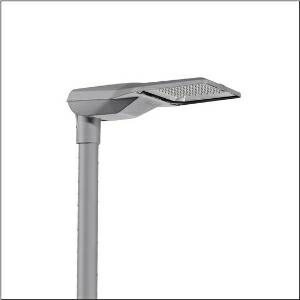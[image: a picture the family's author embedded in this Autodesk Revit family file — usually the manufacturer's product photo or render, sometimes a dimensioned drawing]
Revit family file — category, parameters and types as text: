
# Revit family: streetlight_sl_21_iq_midi___stw1_0a_5xe3e41g08mb_cdbd
name_source: partatom
category: Lighting Fixtures
units: mm (PartAtom-declared; Revit-internal decimal feet)

## family parameters
Cut with Voids When Loaded = No
Host = Face
Light Source = No
Part Type = Normal
Room Calculation Point = No
Round Connector Dimension = Use Diameter
Shared = No

## types (1)
- --- (1 x LED, 20360 lm, 146.7 W, 4000K)
    Apparent Load = 147 VA
    CIE Flux Codes = 38 75 98 100 100
    Color Rendering = 70
    Color Temperature = 4000K
    Default Elevation = 1800 mm
    Description = Streetlight SL 21 iQ midi, mast luminaire, primary light control with lens, of PMMA, primary optical cover: cover, of toughened safety glass, transparent, light distribution: STW1.0a, light emission: direct distribution, primary light characteristic: asymmetric, installation type: post-top, side-entry, LED, High Power LED, rated luminous flux: 20.360lm, luminous efficacy: 139lm/W, light colour: 740, colour temperature: 4000K, control gear: iQ Street-Remote, control: Street-Remote, Auto-Match, Temp-Guard, Lumen-Switch, Night-Set, Smart-Wire, Light-Fading, Desk-Remote (wireless, voltage-free reading and setting of iQ features in the workshop via application-optimized NFC function/RFID function), optimised constant luminous flux control (CLO 2.0), pre-setting: linear dimming characteristic, mains connection: 230..240V, AC, 50/60Hz, start of lifetime: 147W, end of service life: 161W, reduction: 62W, luminaire housing, of diecast aluminium, powder-coated, Siteco® metallic grey (DB 702S), corrosivity category C5 mid according to DIN EN ISO 12944, please order mast flange separately, inclination adjustable: 0°, 5°, 10°, 15°, sealing non-destructively replaceable, multi-level sealing system, length: 644mm, width: 335mm, height: 110mm, mast flange for spigot size: 42mm (side-entry): 5XC10008XM4, 60/48mm (side-entry/post-top): 5XC10108XM2, 76/60mm (side-entry/post-top): 5XC10108XM1, mounting height: 4..8m, protection rating (complete): IP66, insulation class (complete): insulation class II (safety insulation), certification: CE, ENEC, ENEC+, VDE, impact resistance: IK10, permissible operating ambient temperature for outdoor applications: -40..+50°C, standard-compliant lighting for roads and squares, packaging unit: 1 piece

Light Distribution: STW1.0a
    Height = 111 mm
    Lamp = 1 x LED
    Lamp Light Flux = 20360 lm
    Lamp Power = 146.7 W
    Lamp count = 1
    Length = 644 mm
    Luminous efficacy = 139 lm/W
    Manufacturer = Siteco
    ModVariant = No
    Model = 5XE3E41G08MB
    Number of Poles = 1
    OnlyDefault = Yes
    Power Factor = 1
    Product Name = Streetlight SL 21 iQ midi | STW1.0a
    Product group = mast luminaire | pylon top
    ProductGroupID = 6100
    Protection Class = Protection class II
    Protection Degree = IP 66
    RLX_Detail_Level = 1
    RLX_Emergency_Light_Flux = 0 lm
    RLX_Emergency_Type = 0
    RLX_Emergency_Type_DB = No
    RlxData = <blob elided: 26981 chars, md5=238641a8>
    Socket = socket
    Standby Power = 0 W
    System Light Flux = 20360 lm
    System Power = 147 W
    Type Comments = factory setting: luminous flux: 100 % | dim-lin: 254 | 753 mA
    Type Image = l_1004298.jpg
    URL = http://relux.com
    VarID = @adj_188022
    Voltage = 0 V
    Weight = 0.00 kg
    Width = 336 mm

## geometry (parser evidence)
native form markers: Blend x4, Sweep x12
no freeform markers — native parametric forms only
